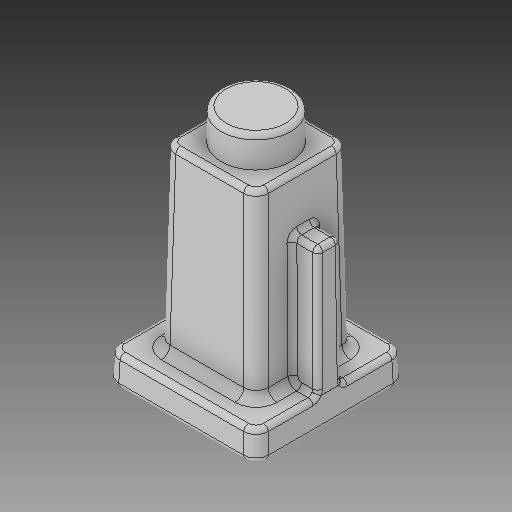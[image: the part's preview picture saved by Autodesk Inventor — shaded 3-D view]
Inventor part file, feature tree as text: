
AUTODESK INVENTOR PART (.ipt)
format: ipt  version: 2019 (Build 230136000, 136)  size: 296,960 bytes
history: native  units: in
note: dims shown in document units (in); Inventor stores cm internally (conversion verified against a paired STEP export)
features: fillet x1
ambient origin geometry x8: Origin, YZ Plane, XZ Plane, XY Plane, X Axis, Y Axis, Z Axis, Center Point
bodies: Solid1 (feature_tree)
feature tree (1):
  fillet  "Fillet5"  [1 undecoded]
note: 1 required parameter value undecoded (feature->parameter linkage not recoverable at this tier; creation-order binding heuristic only, values carry confidence <= 0.55)
